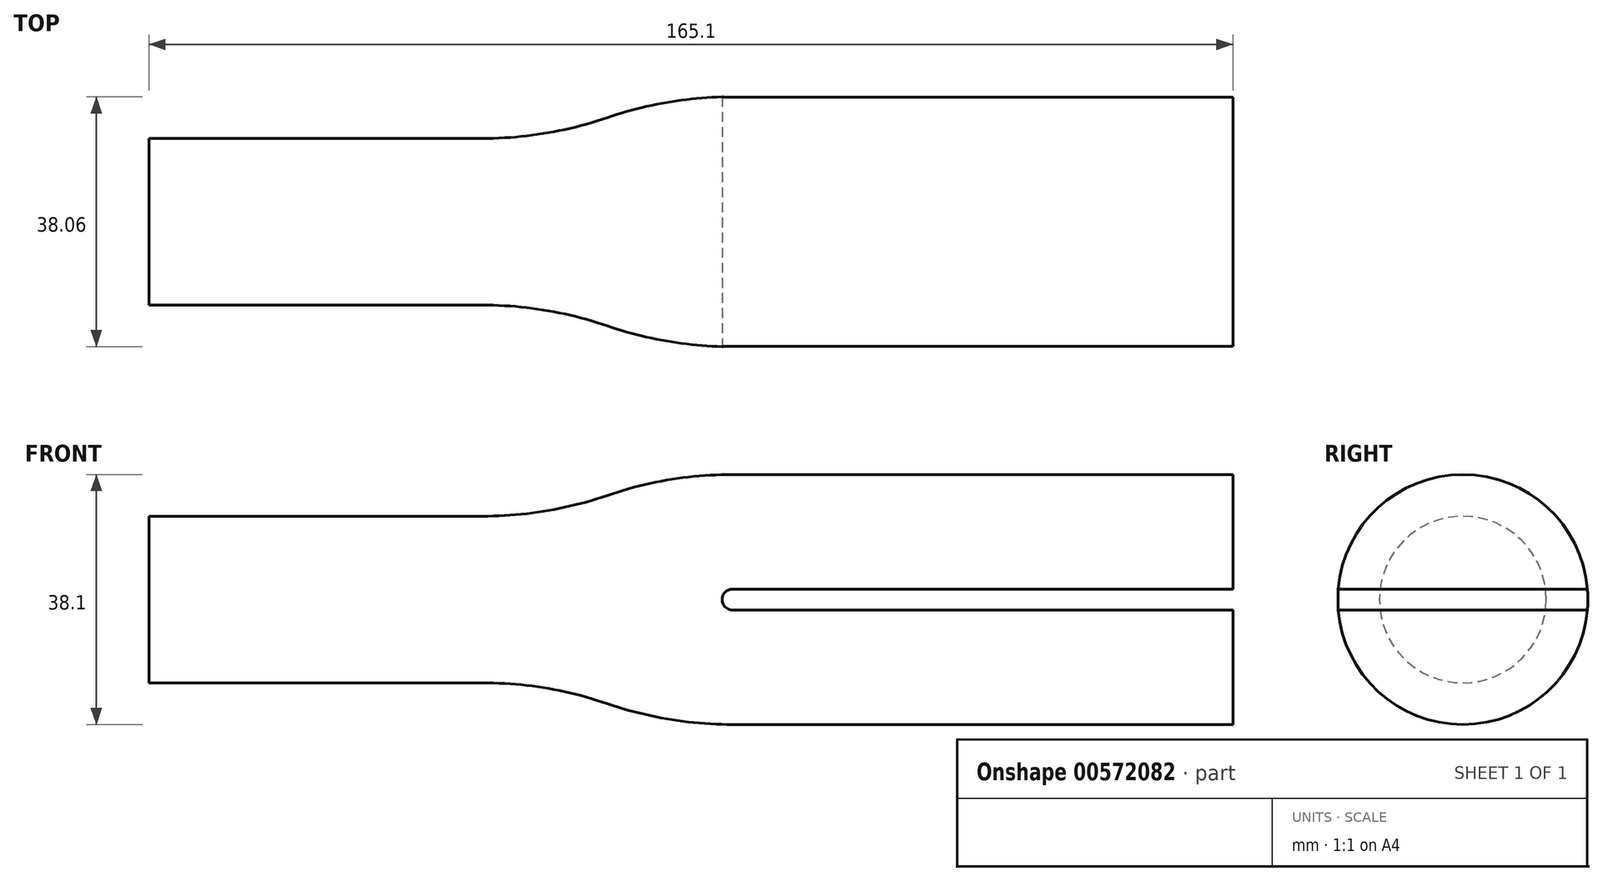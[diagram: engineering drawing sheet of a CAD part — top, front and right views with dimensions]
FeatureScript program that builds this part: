
annotation { "Feature Type Name" : "Feature", "Feature Type Description" : "" }
export const myFeature = defineFeature(function(context is Context, id is Id, definition is map)
    precondition{}
    {
        {
            var Q0;
            Q0=qCreatedBy(makeId("Front.planeOp"),FACE);
            var sketch = newSketch(context, id + "F0", { "sketchPlane" : qUnion([Q0])});
            skLineSegment(sketch, "E0", {"start": v(-88.9, 12.7) * mm, "end": v(-38.1, 12.7) * mm});
            skArc(sketch, "E1", {"start": v(-38.1, 12.7) * mm, "mid": v(-28.44, 13.5) * mm, "end": v(-19.05, 15.88) * mm});
            skArc(sketch, "E2", {"start": v(-19.05, 15.88) * mm, "mid": v(-9.66, 18.25) * mm, "end": v(0, 19.05) * mm});
            skLineSegment(sketch, "E3", {"start": v(0, 19.05) * mm, "end": v(76.2, 19.05) * mm});
            skLineSegment(sketch, "E4", {"start": v(-88.9, 12.7) * mm, "end": v(-88.9, 0) * mm});
            skLineSegment(sketch, "E5", {"start": v(-88.9, 0) * mm, "end": v(76.2, 0) * mm});
            skLineSegment(sketch, "E6", {"start": v(76.2, 0) * mm, "end": v(76.2, 19.05) * mm});
            skSolve(sketch);
        }
        {
            var Q0;
            Q0 = qSketchRegion(id + "F0", true);
            var Q1;
            Q1=sQuery(id+"F0.wireOp",EDGE,"E5");
            revolve(context, id + "F1", {"entities" : qUnion([Q0]), "axis" : qUnion([Q1]), "revolveType" : RevolveType.FULL});
        }
        {
            var Q0;
            Q0=qCreatedBy(makeId("Front.planeOp"),FACE);
            var sketch = newSketch(context, id + "F2", { "sketchPlane" : qUnion([Q0])});
            skLineSegment(sketch, "E7", {"start": v(76.2, 1.59) * mm, "end": v(0, 1.59) * mm});
            skArc(sketch, "E8", {"start": v(0, 1.59) * mm, "mid": v(-1.59, 0) * mm, "end": v(0, -1.59) * mm});
            skLineSegment(sketch, "E9", {"start": v(0, -1.59) * mm, "end": v(76.2, -1.59) * mm});
            skLineSegment(sketch, "E10", {"start": v(76.2, -1.59) * mm, "end": v(76.2, 1.59) * mm});
            skSolve(sketch);
        }
        {
            var Q0;
            Q0 = qSketchRegion(id + "F2", true);
            extrude(context, id + "F3", {"entities" : qUnion([Q0]), "operationType" : NewBodyOperationType.REMOVE, "endBound" : BoundingType.THROUGH_ALL, "oppositeDirection" : true, "depth" : 25.4 * mm, "offsetDistance" : 25.4 * mm, "hasSecondDirection" : true, "secondDirectionBound" : BoundingType.THROUGH_ALL, "secondDirectionOppositeDirection" : false, "secondDirectionDepth" : 25.4 * mm});
        }
    });
